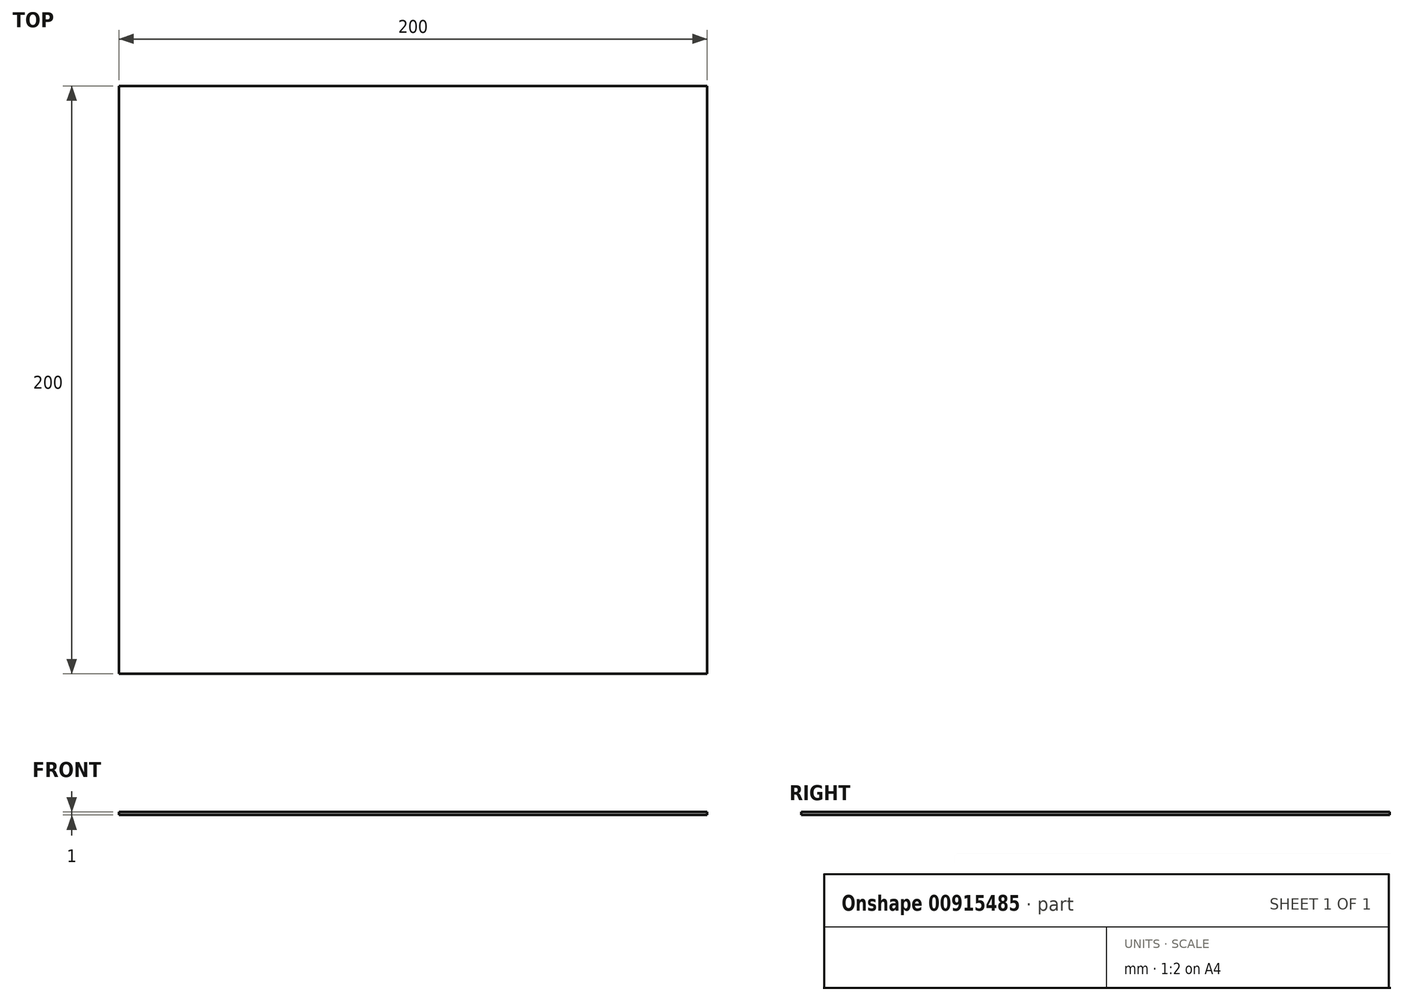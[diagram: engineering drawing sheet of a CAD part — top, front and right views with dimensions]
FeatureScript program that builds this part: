
annotation { "Feature Type Name" : "Feature", "Feature Type Description" : "" }
export const myFeature = defineFeature(function(context is Context, id is Id, definition is map)
    precondition{}
    {
        {
            var Q0;
            Q0=qCreatedBy(makeId("Top.planeOp"),FACE);
            var sketch = newSketch(context, id + "F0", { "sketchPlane" : qUnion([Q0])});
            skLineSegment(sketch, "E0.bottom", {"start": v(-100, 100) * mm, "end": v(100, 100) * mm});
            skLineSegment(sketch, "E0.top", {"start": v(-100, -100) * mm, "end": v(100, -100) * mm});
            skLineSegment(sketch, "E0.left", {"start": v(-100, 100) * mm, "end": v(-100, -100) * mm});
            skLineSegment(sketch, "E0.right", {"start": v(100, 100) * mm, "end": v(100, -100) * mm});
            skPoint(sketch, "E0.middle", {"position": v(0, 0) * mm});
            skSolve(sketch);
        }
        {
            var Q0;
            Q0=makeQuery(id+"F0.imprint","IMPRINT",FACE,{"disambiguationData":[TD([[makeQuery(id+"F0.imprint","IMPRINT",EDGE,{"derivedFrom":sQuery(id+"F0.wireOp",EDGE,"E0.bottom")}),-1.0]])]});
            extrude(context, id + "F1", {"entities" : qUnion([Q0]), "depth" : 1 * mm, "offsetDistance" : 25 * mm});
        }
    });
